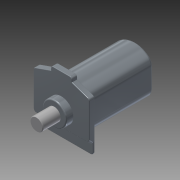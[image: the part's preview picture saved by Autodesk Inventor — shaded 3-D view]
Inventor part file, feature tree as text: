
AUTODESK INVENTOR PART (.ipt)
format: ipt  version: 2016 SP1 (Build 200210100, 210)  size: 268,800 bytes
history: native  units: mm
features: fillet x8, extrude x7, sketch x6, chamfer x2
ambient origin geometry x8: Origin, YZ Plane, XZ Plane, XY Plane, X Axis, Y Axis, Z Axis, Center Point
bodies: Solid1 (feature_tree)
feature tree (23):
  extrude  "Extrusion1"  Depth=55.3mm TaperAngle=0.0deg
  sketch  "Sketch2"  dims[d4=53.2mm d5=11.0mm d6=55.3mm d7=0.0mm d8=2.0mm]
  extrude  "Extrusion2"  Depth=2.0mm
  fillet  "Fillet2"  Radius=55.3mm
  fillet  "Fillet1"  Radius=2.0mm
  extrude  "Extrusion3"  Depth=12.9mm
  fillet  "Fillet3"  Radius=6.4mm
  extrude  "Extrusion4"  Depth=2.0mm
  extrude  "Extrusion5"  Depth=1.5mm TaperAngle=0.0deg
  chamfer  "Chamfer1"  Distance=4.5mm
  fillet  "Fillet4"  Radius=2.0mm
  fillet  "Fillet5"  Radius=2.0mm
  fillet  "Fillet6"  Radius=0.5mm
  fillet  "Fillet7"  Radius=45.0mm
  extrude  "Extrusion6"  Depth=2.0mm
  extrude  "Extrusion7"  Depth=2.0mm
  fillet  "Fillet8"  Radius=19.3mm
  chamfer  "Chamfer2"  Distance=5.7mm
  sketch  "Sketch1"  dims[d0=36.0mm d1=55.3mm d2=0.0mm]
  sketch  "Sketch3"  dims[d9=8.0mm d10=12.9mm d11=6.4mm d12=0.0mm]
  sketch  "Sketch4"  dims[d13=0.9mm d15=2.0mm]
  sketch  "Sketch5"  dims[d16=2.0mm d17=1.5mm d18=0.0mm d19=4.5mm d20=0.0mm]
  sketch  "Sketch6"  dims[d21=3.0mm d22=2.0mm d23=45.0deg d24=2.0mm d25=2.0mm d26=0.5mm d28=45.0mm d29=17.0mm d30=2.0mm d31=19.3mm d32=5.7mm d33=0.0mm d34=10.5mm d35=14.3mm d36=0.0mm d37=1.0mm d38=0.5mm d39=2.0mm d40=45.0deg]
